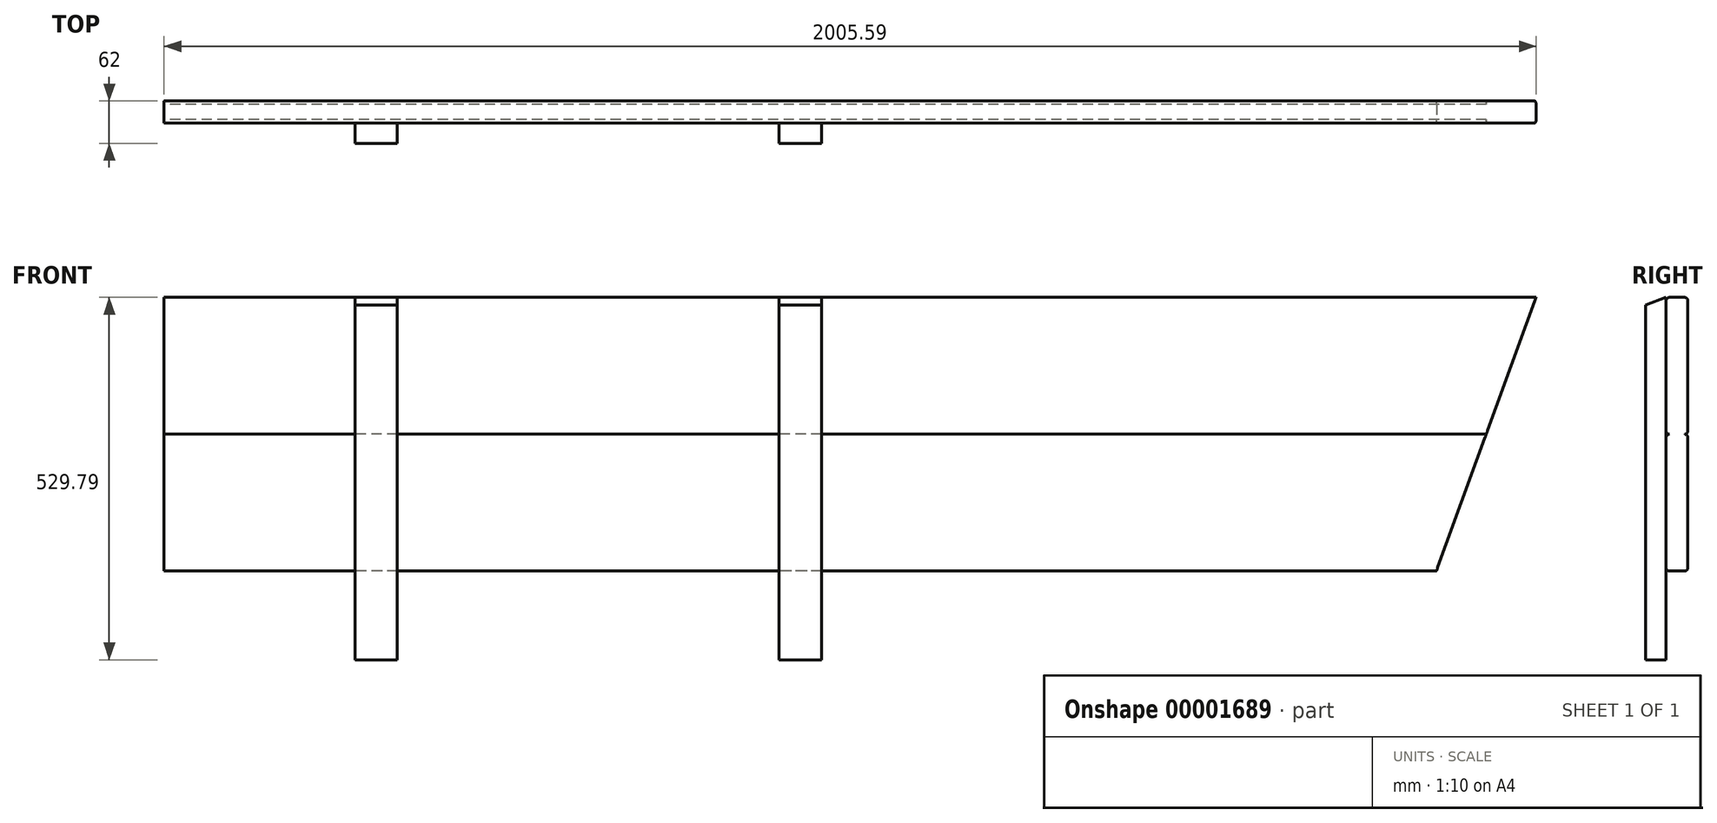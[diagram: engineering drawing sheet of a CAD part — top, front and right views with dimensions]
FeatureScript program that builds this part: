
annotation { "Feature Type Name" : "Feature", "Feature Type Description" : "" }
export const myFeature = defineFeature(function(context is Context, id is Id, definition is map)
    precondition{}
    {
        {
            var Q0;
            Q0=qCreatedBy(makeId("Right.planeOp"),FACE);
            var sketch = newSketch(context, id + "F0", { "sketchPlane" : qUnion([Q0])});
            skLineSegment(sketch, "E0.bottom", {"start": v(5, 0) * mm, "end": v(27, 0) * mm});
            skLineSegment(sketch, "E0.top", {"start": v(5, 200) * mm, "end": v(27, 200) * mm});
            skLineSegment(sketch, "E0.left", {"start": v(0, 5) * mm, "end": v(0, 195) * mm});
            skLineSegment(sketch, "E0.right", {"start": v(32, 5) * mm, "end": v(32, 195) * mm});
            skPoint(sketch, "E1.visualSharp", {"position": v(32, 200) * mm});
            skArc(sketch, "E1.filletArc", {"start": v(32, 195) * mm, "mid": v(30.54, 198.54) * mm, "end": v(27, 200) * mm});
            skPoint(sketch, "E2.visualSharp", {"position": v(0, 200) * mm});
            skArc(sketch, "E2.filletArc", {"start": v(5, 200) * mm, "mid": v(1.46, 198.54) * mm, "end": v(0, 195) * mm});
            skPoint(sketch, "E3.visualSharp", {"position": v(32, 0) * mm});
            skArc(sketch, "E3.filletArc", {"start": v(27, 0) * mm, "mid": v(30.54, 1.46) * mm, "end": v(32, 5) * mm});
            skPoint(sketch, "E4.visualSharp", {"position": v(0, 0) * mm});
            skArc(sketch, "E4.filletArc", {"start": v(0, 5) * mm, "mid": v(1.46, 1.46) * mm, "end": v(5, 0) * mm});
            skLineSegment(sketch, "E5.top", {"start": v(5, 400) * mm, "end": v(27, 400) * mm});
            skLineSegment(sketch, "E5.left", {"start": v(0, 205) * mm, "end": v(0, 395) * mm});
            skLineSegment(sketch, "E5.right", {"start": v(32, 205) * mm, "end": v(32, 395) * mm});
            skArc(sketch, "E6.filletArc", {"start": v(27, 200) * mm, "mid": v(30.54, 201.46) * mm, "end": v(32, 205) * mm});
            skArc(sketch, "E7.filletArc", {"start": v(0, 205) * mm, "mid": v(1.46, 201.46) * mm, "end": v(5, 200) * mm});
            skPoint(sketch, "E8.visualSharp", {"position": v(32, 400) * mm});
            skArc(sketch, "E8.filletArc", {"start": v(32, 395) * mm, "mid": v(30.54, 398.54) * mm, "end": v(27, 400) * mm});
            skPoint(sketch, "E9.visualSharp", {"position": v(0, 400) * mm});
            skArc(sketch, "E9.filletArc", {"start": v(5, 400) * mm, "mid": v(1.46, 398.54) * mm, "end": v(0, 395) * mm});
            skSolve(sketch);
        }
        {
            var Q0;
            Q0=makeQuery(id+"F0.imprint","IMPRINT",FACE,{"disambiguationData":[TD([[makeQuery(id+"F0.imprint","IMPRINT",EDGE,{"derivedFrom":sQuery(id+"F0.wireOp",EDGE,"E0.top")}),1.0]])]});
            var Q1;
            Q1=makeQuery(id+"F0.imprint","IMPRINT",FACE,{"disambiguationData":[TD([[makeQuery(id+"F0.imprint","IMPRINT",EDGE,{"derivedFrom":sQuery(id+"F0.wireOp",EDGE,"E0.bottom")}),1.0]])]});
            extrude(context, id + "F1", {"entities" : qUnion([Q0, Q1]), "depth" : 1240 * mm});
        }
        {
            var Q0;
            Q0=makeQuery(id+"F1.opExtrude","CAP_FACE",FACE,{"disambiguationData":[OSD([sQuery(id+"F0.wireOp",EDGE,"E0.bottom"),sQuery(id+"F0.wireOp",EDGE,"E0.left"),sQuery(id+"F0.wireOp",EDGE,"E0.right"),sQuery(id+"F0.wireOp",EDGE,"E1.filletArc"),sQuery(id+"F0.wireOp",EDGE,"E2.filletArc"),sQuery(id+"F0.wireOp",EDGE,"E3.filletArc"),sQuery(id+"F0.wireOp",EDGE,"E4.filletArc"),sQuery(id+"F0.wireOp",EDGE,"E5.top"),sQuery(id+"F0.wireOp",EDGE,"E5.left"),sQuery(id+"F0.wireOp",EDGE,"E5.right"),sQuery(id+"F0.wireOp",EDGE,"E6.filletArc"),sQuery(id+"F0.wireOp",EDGE,"E7.filletArc"),sQuery(id+"F0.wireOp",EDGE,"E8.filletArc"),sQuery(id+"F0.wireOp",EDGE,"E9.filletArc")])],"isStart":true});
            cPlane(context, id + "F2", {"entities" : qUnion([Q0]), "cplaneType" : CPlaneType.OFFSET, "offset" : 620 * mm, "oppositeDirection" : true, "width" : 150 * mm, "height" : 150 * mm});
        }
        {
            var Q0;
            Q0=makeQuery(id+"F1.opExtrude","SWEPT_FACE",FACE,{"disambiguationData":[OSD([sQuery(id+"F0.wireOp",EDGE,"E5.top")])]});
            var sketch = newSketch(context, id + "F3", { "sketchPlane" : qUnion([Q0])});
            skLineSegment(sketch, "E10.bottom", {"start": v(279, -30) * mm, "end": v(341, -30) * mm});
            skLineSegment(sketch, "E10.top", {"start": v(279, 0) * mm, "end": v(341, 0) * mm});
            skLineSegment(sketch, "E10.left", {"start": v(279, -30) * mm, "end": v(279, 0) * mm});
            skLineSegment(sketch, "E10.right", {"start": v(341, -30) * mm, "end": v(341, 0) * mm});
            skLineSegment(sketch, "E11", {"start": v(310, -30) * mm, "end": v(310, 0) * mm});
            skSolve(sketch);
        }
        {
            var Q0;
            {var subQ2=sQuery(id+"F3.wireOp",EDGE,"E10.left");var subQ7=sQuery(id+"F3.wireOp",EDGE,"E10.right");Q0=qUnion([makeQuery(id+"F3.imprint","IMPRINT",FACE,{"disambiguationData":[TD([[makeQuery(id+"F3.imprint","IMPRINT",EDGE,{"derivedFrom":subQ2}),-1.0]])]}),makeQuery(id+"F3.imprint","IMPRINT",FACE,{"disambiguationData":[TD([[makeQuery(id+"F3.imprint","IMPRINT",EDGE,{"derivedFrom":subQ7}),1.0]])]})]);}
            extrude(context, id + "F4", {"entities" : qUnion([Q0]), "oppositeDirection" : true, "depth" : 529.8 * mm});
        }
        {
            var Q0;
            Q0=makeQuery(id+"F4.opExtrude","SWEPT_FACE",FACE,{"disambiguationData":[OSD([sQuery(id+"F3.wireOp",EDGE,"E10.left")])]});
            var sketch = newSketch(context, id + "F5", { "sketchPlane" : qUnion([Q0])});
            skLineSegment(sketch, "E12", {"start": v(0, 400) * mm, "end": v(30, 389.08) * mm});
            skSolve(sketch);
        }
        {
            var Q0;
            Q0=qSketchRegion(id+"F5",true);
            var Q1;
            {var subQ2=sQuery(id+"F5.wireOp",EDGE,"E12");Q1=makeQuery(id+"F5.imprint","IMPRINT",FACE,{"disambiguationData":[TD([[makeQuery(id+"F5.imprint","IMPRINT",EDGE,{"derivedFrom":subQ2}),1.0]])]});}
            extrude(context, id + "F6", {"entities" : qUnion([Q0, Q1]), "operationType" : NewBodyOperationType.REMOVE, "endBound" : BoundingType.THROUGH_ALL, "oppositeDirection" : true, "depth" : 25 * mm});
        }
        {
            var Q0;
            Q0=makeQuery(id+"F4.opExtrude","SWEPT_BODY",BODY,{"disambiguationData":[OSD([sQuery(id+"F3.wireOp",EDGE,"E10.bottom"),sQuery(id+"F3.wireOp",EDGE,"E10.top"),sQuery(id+"F3.wireOp",EDGE,"E10.left"),sQuery(id+"F3.wireOp",EDGE,"E10.right")])]});
            var Q1;
            Q1=qCreatedBy(id+"F2.planeOp",FACE);
            mirror(context, id + "F7", {"entities" : qUnion([Q0]), "mirrorPlane" : qUnion([Q1])});
        }
        {
            var Q0;
            Q0=makeQuery(id+"F1.opExtrude","CAP_FACE",FACE,{"disambiguationData":[OSD([sQuery(id+"F0.wireOp",EDGE,"E0.bottom"),sQuery(id+"F0.wireOp",EDGE,"E0.left"),sQuery(id+"F0.wireOp",EDGE,"E0.right"),sQuery(id+"F0.wireOp",EDGE,"E1.filletArc"),sQuery(id+"F0.wireOp",EDGE,"E2.filletArc"),sQuery(id+"F0.wireOp",EDGE,"E3.filletArc"),sQuery(id+"F0.wireOp",EDGE,"E4.filletArc"),sQuery(id+"F0.wireOp",EDGE,"E5.top"),sQuery(id+"F0.wireOp",EDGE,"E5.left"),sQuery(id+"F0.wireOp",EDGE,"E5.right"),sQuery(id+"F0.wireOp",EDGE,"E6.filletArc"),sQuery(id+"F0.wireOp",EDGE,"E7.filletArc"),sQuery(id+"F0.wireOp",EDGE,"E8.filletArc"),sQuery(id+"F0.wireOp",EDGE,"E9.filletArc")])],"isStart":false});
            extrude(context, id + "F8", {"entities" : qUnion([Q0]), "operationType" : NewBodyOperationType.ADD, "depth" : 620 * mm});
        }
        {
            var Q0;
            Q0=makeQuery(id+"F8.opExtrude","CAP_FACE",FACE,{"disambiguationData":[OSD([sQuery(id+"F0.wireOp",EDGE,"E0.bottom"),sQuery(id+"F0.wireOp",EDGE,"E0.left"),sQuery(id+"F0.wireOp",EDGE,"E0.right"),sQuery(id+"F0.wireOp",EDGE,"E1.filletArc"),sQuery(id+"F0.wireOp",EDGE,"E2.filletArc"),sQuery(id+"F0.wireOp",EDGE,"E3.filletArc"),sQuery(id+"F0.wireOp",EDGE,"E4.filletArc"),sQuery(id+"F0.wireOp",EDGE,"E5.top"),sQuery(id+"F0.wireOp",EDGE,"E5.left"),sQuery(id+"F0.wireOp",EDGE,"E5.right"),sQuery(id+"F0.wireOp",EDGE,"E6.filletArc"),sQuery(id+"F0.wireOp",EDGE,"E7.filletArc"),sQuery(id+"F0.wireOp",EDGE,"E8.filletArc"),sQuery(id+"F0.wireOp",EDGE,"E9.filletArc")])],"isStart":false});
            extrude(context, id + "F9", {"entities" : qUnion([Q0]), "operationType" : NewBodyOperationType.ADD, "depth" : 500 * mm});
        }
        {
            var Q0;
            {var subQ0=sQuery(id+"F0.wireOp",EDGE,"E0.left");Q0=makeQuery(id+"F9.boolean.opBoolean","MERGE",FACE,{"derivedFrom":[makeQuery(id+"F8.boolean.opBoolean","MERGE",FACE,{"derivedFrom":[makeQuery(id+"F1.opExtrude","SWEPT_FACE",FACE,{"disambiguationData":[OSD([subQ0])]}),makeQuery(id+"F8.opExtrude","SWEPT_FACE",FACE,{"disambiguationData":[OSD([subQ0])]})]}),makeQuery(id+"F9.opExtrude","SWEPT_FACE",FACE,{"disambiguationData":[OSD([subQ0])]})]});}
            var sketch = newSketch(context, id + "F10", { "sketchPlane" : qUnion([Q0])});
            skLineSegment(sketch, "E13", {"start": v(1860, 0) * mm, "end": v(2360, 1373.74) * mm});
            skLineSegment(sketch, "E14", {"start": v(2360, 1373.74) * mm, "end": v(2788.66, 1373.74) * mm});
            skLineSegment(sketch, "E15", {"start": v(2788.66, 1373.74) * mm, "end": v(2788.66, 0) * mm});
            skLineSegment(sketch, "E16", {"start": v(2788.66, 0) * mm, "end": v(1860, 0) * mm});
            skSolve(sketch);
        }
        {
            var Q0;
            {var subQ0=sQuery(id+"F0.wireOp",EDGE,"E0.left");var subQ5=makeQuery(id+"F9.opExtrude","CAP_EDGE",EDGE,{"disambiguationData":[OSD([subQ0])],"isStart":false});var subQ7=makeQuery(id+"F10.imprint","IMPRINT",EDGE,{"derivedFrom":subQ5});var subQ13=sQuery(id+"F10.wireOp",EDGE,"E14");Q0=qUnion([makeQuery(id+"F10.imprint","IMPRINT",FACE,{"disambiguationData":[TD([[makeQuery(id+"F10.imprint","IMPRINT",EDGE,{"derivedFrom":subQ13}),-1.0]])]}),makeQuery(id+"F10.imprint","IMPRINT",FACE,{"disambiguationData":[TD([[subQ7,1.0]])]})]);}
            extrude(context, id + "F11", {"entities" : qUnion([Q0]), "operationType" : NewBodyOperationType.REMOVE, "endBound" : BoundingType.THROUGH_ALL, "oppositeDirection" : true, "depth" : 25 * mm});
        }
    });
